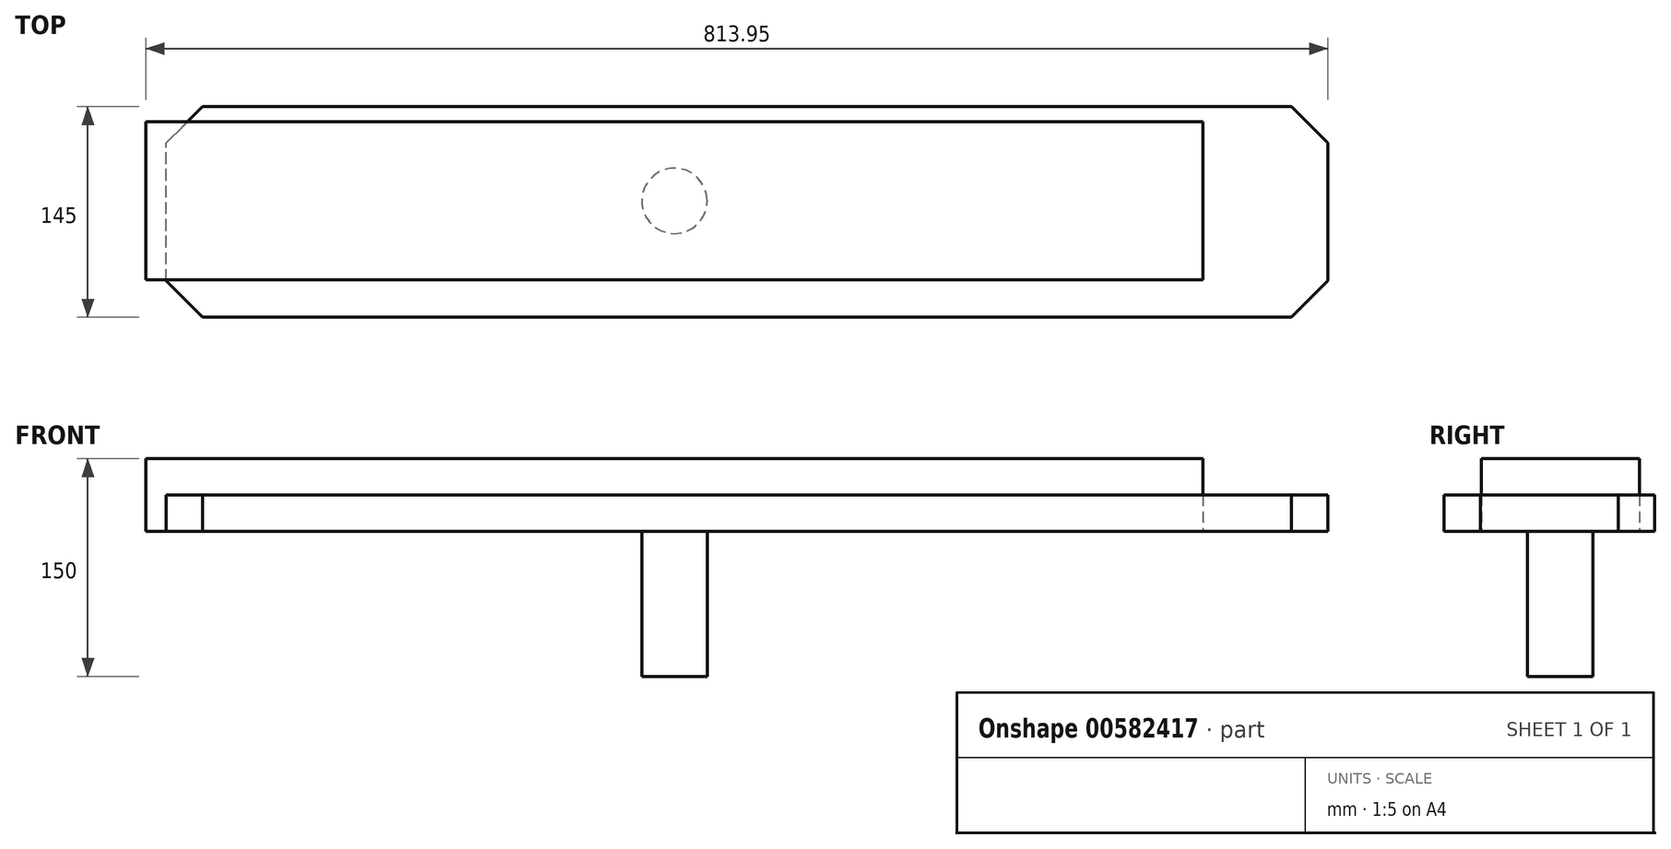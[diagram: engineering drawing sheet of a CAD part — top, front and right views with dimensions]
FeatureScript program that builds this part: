
annotation { "Feature Type Name" : "Feature", "Feature Type Description" : "" }
export const myFeature = defineFeature(function(context is Context, id is Id, definition is map)
    precondition{}
    {
        {
            var Q0;
            Q0=qCreatedBy(makeId("Top.planeOp"),FACE);
            var sketch = newSketch(context, id + "F0", { "sketchPlane" : qUnion([Q0])});
            skLineSegment(sketch, "E0.bottom", {"start": v(-384.42, -151.84) * mm, "end": v(415.58, -151.84) * mm});
            skLineSegment(sketch, "E0.top", {"start": v(-384.42, -6.84) * mm, "end": v(415.58, -6.84) * mm});
            skLineSegment(sketch, "E0.left", {"start": v(-384.42, -151.84) * mm, "end": v(-384.42, -6.84) * mm});
            skLineSegment(sketch, "E0.right", {"start": v(415.58, -151.84) * mm, "end": v(415.58, -6.84) * mm});
            skSolve(sketch);
        }
        {
            var Q0;
            Q0=qCreatedBy(makeId("Top.planeOp"),FACE);
            var sketch = newSketch(context, id + "F1", { "sketchPlane" : qUnion([Q0])});
            skLineSegment(sketch, "E1.bottom", {"start": v(-398.37, -126.22) * mm, "end": v(329.63, -126.22) * mm});
            skLineSegment(sketch, "E1.top", {"start": v(-398.37, -17.22) * mm, "end": v(329.63, -17.22) * mm});
            skLineSegment(sketch, "E1.left", {"start": v(-398.37, -126.22) * mm, "end": v(-398.37, -17.22) * mm});
            skLineSegment(sketch, "E1.right", {"start": v(329.63, -126.22) * mm, "end": v(329.63, -17.22) * mm});
            skCircle(sketch, "E2", {"center": v(-34.37, -71.72) * mm, "radius": 22.5 * mm});
            skPoint(sketch, "E3", {"position": v(-34.37, -17.22) * mm});
            skPoint(sketch, "E4", {"position": v(-34.37, -126.22) * mm});
            skLineSegment(sketch, "E5", {"start": v(-34.37, -17.22) * mm, "end": v(-34.37, -126.22) * mm, "construction": true});
            skSolve(sketch);
        }
        {
            var Q0;
            Q0=makeQuery(id+"F1.imprint","IMPRINT",FACE,{"disambiguationData":[TD([[makeQuery(id+"F1.imprint","IMPRINT",EDGE,{"derivedFrom":sQuery(id+"F1.wireOp",EDGE,"E1.bottom")}),1.0]])]});
            var Q1;
            Q1=makeQuery(id+"F1.imprint","IMPRINT",FACE,{"disambiguationData":[TD([[makeQuery(id+"F1.imprint","IMPRINT",EDGE,{"derivedFrom":sQuery(id+"F1.wireOp",EDGE,"E2")}),1.0]])]});
            extrude(context, id + "F2", {"entities" : qUnion([Q0, Q1]), "depth" : 50 * mm});
        }
        {
            var Q0;
            Q0=makeQuery(id+"F1.imprint","IMPRINT",FACE,{"disambiguationData":[TD([[makeQuery(id+"F1.imprint","IMPRINT",EDGE,{"derivedFrom":sQuery(id+"F1.wireOp",EDGE,"E2")}),1.0]])]});
            extrude(context, id + "F3", {"entities" : qUnion([Q0]), "operationType" : NewBodyOperationType.ADD, "oppositeDirection" : true, "depth" : 100 * mm});
        }
        {
            var Q0;
            Q0=qSketchRegion(id+"F0",true);
            extrude(context, id + "F4", {"entities" : qUnion([Q0]), "depth" : 25 * mm});
        }
        {
            var Q0;
            Q0=makeQuery(id+"F4.opExtrude","SWEPT_EDGE",EDGE,{"disambiguationData":[OSD([sQuery(id+"F0.wireOp",EDGE,"E0.top"),sQuery(id+"F0.wireOp",EDGE,"E0.right")])]});
            var Q1;
            Q1=makeQuery(id+"F4.opExtrude","SWEPT_EDGE",EDGE,{"disambiguationData":[OSD([sQuery(id+"F0.wireOp",EDGE,"E0.bottom"),sQuery(id+"F0.wireOp",EDGE,"E0.right")])]});
            var Q2;
            Q2=makeQuery(id+"F4.opExtrude","SWEPT_EDGE",EDGE,{"disambiguationData":[OSD([sQuery(id+"F0.wireOp",EDGE,"E0.top"),sQuery(id+"F0.wireOp",EDGE,"E0.left")])]});
            var Q3;
            Q3=makeQuery(id+"F4.opExtrude","SWEPT_EDGE",EDGE,{"disambiguationData":[OSD([sQuery(id+"F0.wireOp",EDGE,"E0.bottom"),sQuery(id+"F0.wireOp",EDGE,"E0.left")])]});
            chamfer(context, id + "F5", {"entities" : qUnion([Q0, Q1, Q2, Q3]), "width" : 25 * mm, "tangentPropagation" : true});
        }
    });
